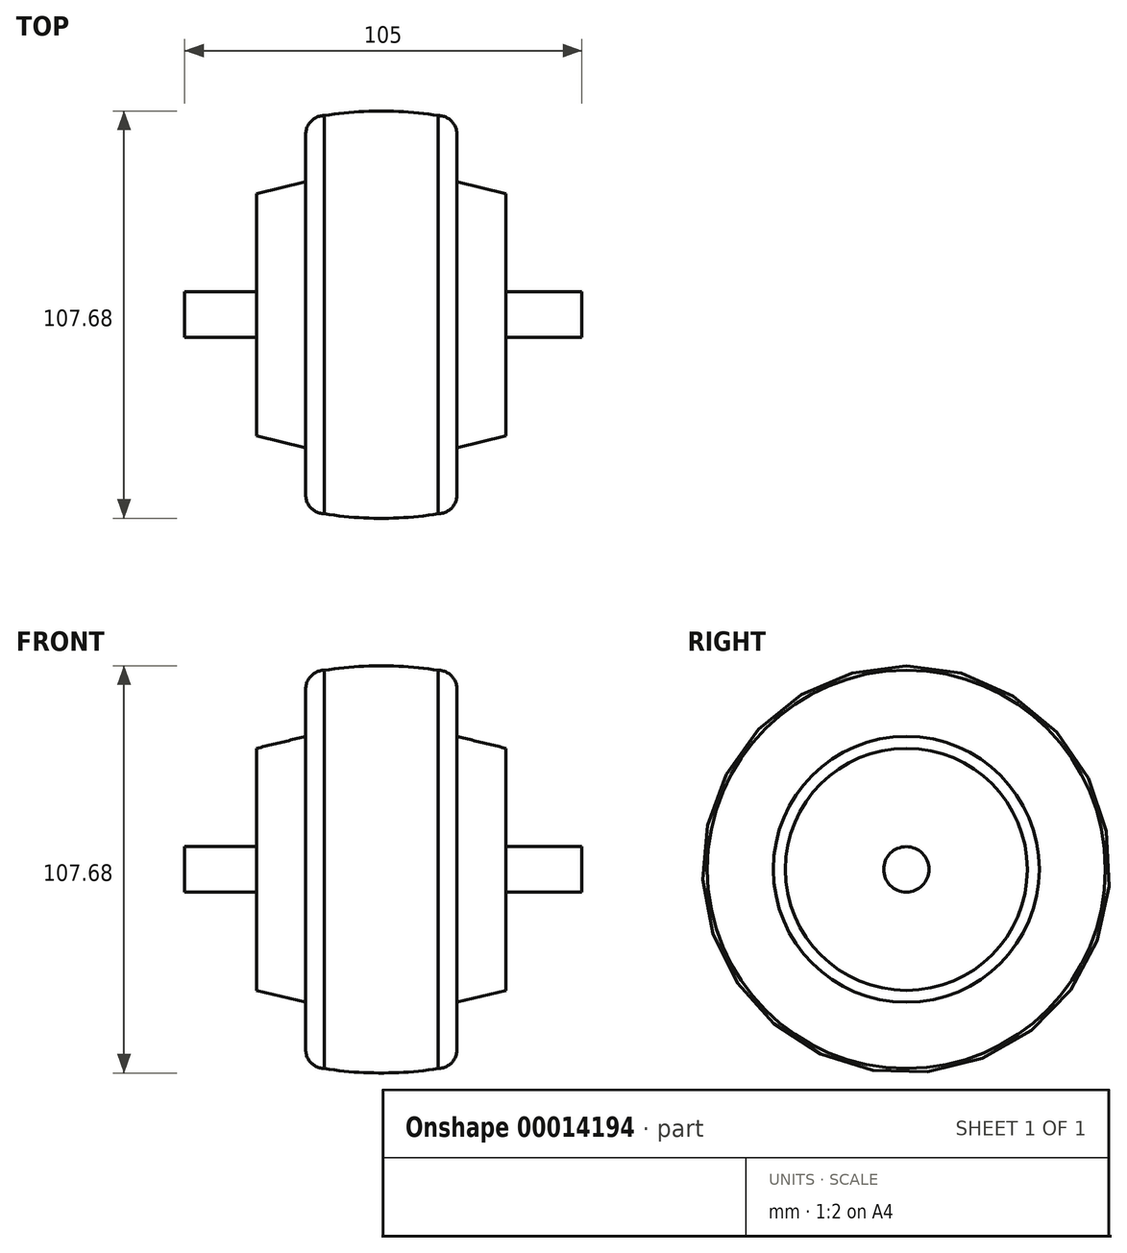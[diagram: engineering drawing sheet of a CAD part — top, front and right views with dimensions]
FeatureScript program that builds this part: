
annotation { "Feature Type Name" : "Feature", "Feature Type Description" : "" }
export const myFeature = defineFeature(function(context is Context, id is Id, definition is map)
    precondition{}
    {
        {
            var Q0;
            Q0=qCreatedBy(makeId("Top.planeOp"),FACE);
            var sketch = newSketch(context, id + "F0", { "sketchPlane" : qUnion([Q0])});
            skLineSegment(sketch, "E0.left", {"start": v(-20, 35.16) * mm, "end": v(-20, 47.66) * mm});
            skLineSegment(sketch, "E0.right", {"start": v(20, 35.16) * mm, "end": v(20, 47.66) * mm});
            skLineSegment(sketch, "E1.right", {"start": v(-33, 0) * mm, "end": v(-33, 32) * mm});
            skLineSegment(sketch, "E2.MirrorCS", {"start": v(33, 0) * mm, "end": v(33, 32) * mm});
            skLineSegment(sketch, "E3", {"start": v(-20, 35.16) * mm, "end": v(-33, 32) * mm});
            skLineSegment(sketch, "E4.MirrorCS", {"start": v(20, 35.16) * mm, "end": v(33, 32) * mm});
            skPoint(sketch, "E5.MirrorCS.end.orphan", {"position": v(29.15, 0) * mm});
            skArc(sketch, "E6.filletArc", {"start": v(-15.04, 52.66) * mm, "mid": v(-18.55, 51.18) * mm, "end": v(-20, 47.66) * mm});
            skArc(sketch, "E7.filletArc", {"start": v(20, 47.66) * mm, "mid": v(18.55, 51.18) * mm, "end": v(15.04, 52.66) * mm});
            skLineSegment(sketch, "E8", {"start": v(-33, 0) * mm, "end": v(33, 0) * mm});
            skArc(sketch, "E9", {"start": v(15.04, 52.66) * mm, "mid": v(0, 53.84) * mm, "end": v(-15.04, 52.66) * mm});
            skSolve(sketch);
        }
        {
            var Q0;
            Q0=qSketchRegion(id+"F0",true);
            var Q1;
            Q1=sQuery(id+"F0.wireOp",EDGE,"E8");
            revolve(context, id + "F1", {"entities" : qUnion([Q0]), "axis" : qUnion([Q1]), "revolveType" : RevolveType.FULL});
        }
        {
            var Q0;
            Q0=makeQuery(id+"F1.opRevolve","SWEPT_FACE",FACE,{"disambiguationData":[OSD([sQuery(id+"F0.wireOp",EDGE,"E2.MirrorCS")])]});
            var sketch = newSketch(context, id + "F2", { "sketchPlane" : qUnion([Q0])});
            skCircle(sketch, "E10", {"center": v(0, 0) * mm, "radius": 6 * mm});
            skSolve(sketch);
        }
        {
            var Q0;
            Q0=qSketchRegion(id+"F2",true);
            extrude(context, id + "F3", {"entities" : qUnion([Q0]), "operationType" : NewBodyOperationType.ADD, "depth" : 20 * mm, "hasSecondDirection" : true, "secondDirectionOppositeDirection" : true, "secondDirectionDepth" : 85 * mm});
        }
    });
